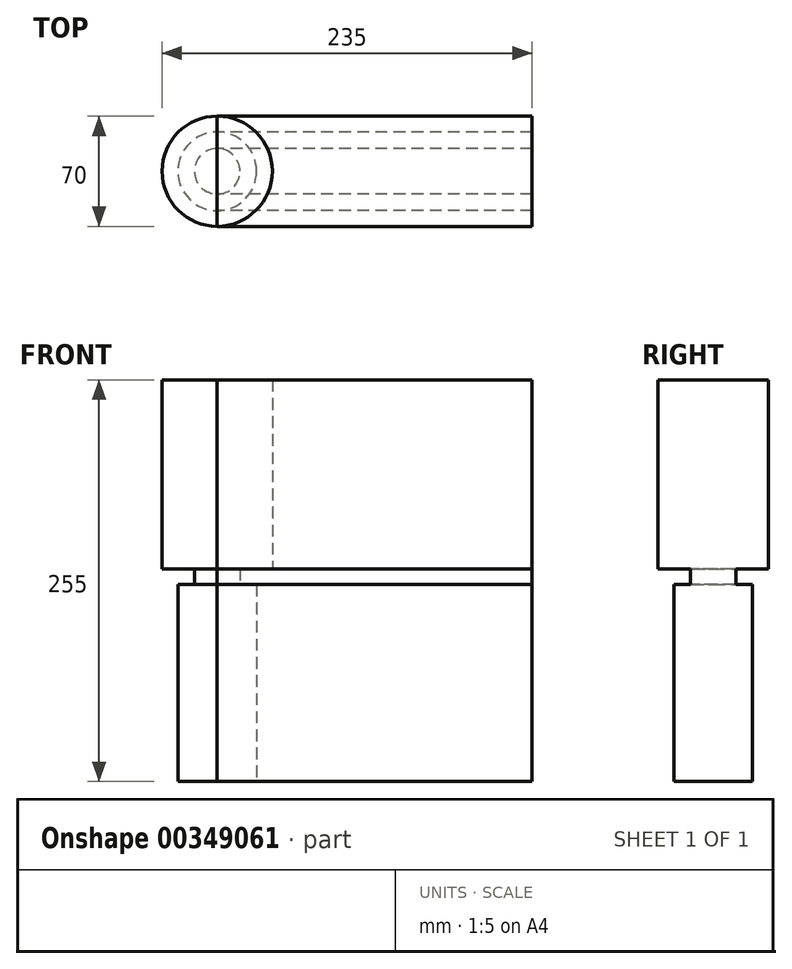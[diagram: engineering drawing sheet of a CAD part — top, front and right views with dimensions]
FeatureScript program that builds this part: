
annotation { "Feature Type Name" : "Feature", "Feature Type Description" : "" }
export const myFeature = defineFeature(function(context is Context, id is Id, definition is map)
    precondition{}
    {
        {
            var Q0;
            Q0=qCreatedBy(makeId("Top.planeOp"),FACE);
            var sketch = newSketch(context, id + "F0", { "sketchPlane" : qUnion([Q0])});
            skCircle(sketch, "E0", {"center": v(0, 0) * mm, "radius": 25 * mm});
            skSolve(sketch);
        }
        {
            var Q0;
            Q0=qSketchRegion(id+"F0",true);
            extrude(context, id + "F1", {"entities" : qUnion([Q0]), "depth" : 125 * mm, "offsetDistance" : 25 * mm});
        }
        {
            var Q0;
            Q0=makeQuery(id+"F1.opExtrude","CAP_FACE",FACE,{"disambiguationData":[OSD([sQuery(id+"F0.wireOp",EDGE,"E0")])],"isStart":false});
            var sketch = newSketch(context, id + "F2", { "sketchPlane" : qUnion([Q0])});
            skCircle(sketch, "E1", {"center": v(0, 0) * mm, "radius": 14.5 * mm});
            skSolve(sketch);
        }
        {
            var Q0;
            Q0=qSketchRegion(id+"F2",true);
            extrude(context, id + "F3", {"entities" : qUnion([Q0]), "operationType" : NewBodyOperationType.ADD, "depth" : 10 * mm, "offsetDistance" : 25 * mm});
        }
        {
            var Q0;
            Q0=makeQuery(id+"F3.opExtrude","CAP_FACE",FACE,{"disambiguationData":[OSD([sQuery(id+"F2.wireOp",EDGE,"E1")])],"isStart":false});
            var sketch = newSketch(context, id + "F4", { "sketchPlane" : qUnion([Q0])});
            skCircle(sketch, "E2", {"center": v(0, 0) * mm, "radius": 35 * mm});
            skSolve(sketch);
        }
        {
            var Q0;
            Q0=qSketchRegion(id+"F4",true);
            extrude(context, id + "F5", {"entities" : qUnion([Q0]), "operationType" : NewBodyOperationType.ADD, "depth" : 120 * mm, "offsetDistance" : 25 * mm});
        }
        {
            var Q0;
            Q0=qCreatedBy(makeId("Right.planeOp"),FACE);
            var sketch = newSketch(context, id + "F6", { "sketchPlane" : qUnion([Q0])});
            skLineSegment(sketch, "E3.0", {"start": v(-35, 135) * mm, "end": v(35, 135) * mm});
            skLineSegment(sketch, "E4.0", {"start": v(-35, 255) * mm, "end": v(35, 255) * mm});
            skLineSegment(sketch, "E5.0", {"start": v(-25, 125) * mm, "end": v(25, 125) * mm});
            skLineSegment(sketch, "E6.0", {"start": v(-25, 0) * mm, "end": v(25, 0) * mm});
            skLineSegment(sketch, "E7.0", {"start": v(-14.5, 125) * mm, "end": v(14.5, 125) * mm});
            skLineSegment(sketch, "E8.0", {"start": v(-14.5, 135) * mm, "end": v(14.5, 135) * mm});
            skLineSegment(sketch, "E9", {"start": v(35, 135) * mm, "end": v(14.5, 135) * mm});
            skLineSegment(sketch, "E10", {"start": v(14.5, 125) * mm, "end": v(25, 125) * mm});
            skLineSegment(sketch, "E11", {"start": v(25, 0) * mm, "end": v(-25, 0) * mm});
            skLineSegment(sketch, "E12", {"start": v(-25, 125) * mm, "end": v(-14.5, 125) * mm});
            skLineSegment(sketch, "E13", {"start": v(-14.5, 135) * mm, "end": v(-35, 135) * mm});
            skLineSegment(sketch, "E14", {"start": v(35, 255) * mm, "end": v(35, 135) * mm});
            skLineSegment(sketch, "E15", {"start": v(-35, 255) * mm, "end": v(-35, 135) * mm});
            skLineSegment(sketch, "E16", {"start": v(-25, 125) * mm, "end": v(-25, 0) * mm});
            skLineSegment(sketch, "E17", {"start": v(-14.5, 135) * mm, "end": v(-14.5, 125) * mm});
            skLineSegment(sketch, "E18", {"start": v(14.5, 135) * mm, "end": v(14.5, 125) * mm});
            skLineSegment(sketch, "E19", {"start": v(25, 125) * mm, "end": v(25, 0) * mm});
            skSolve(sketch);
        }
        {
            var Q0;
            Q0 = qSketchRegion(id + "F6", true);
            extrude(context, id + "F7", {"entities" : qUnion([Q0]), "depth" : 200 * mm, "offsetDistance" : 25 * mm});
        }
    });
